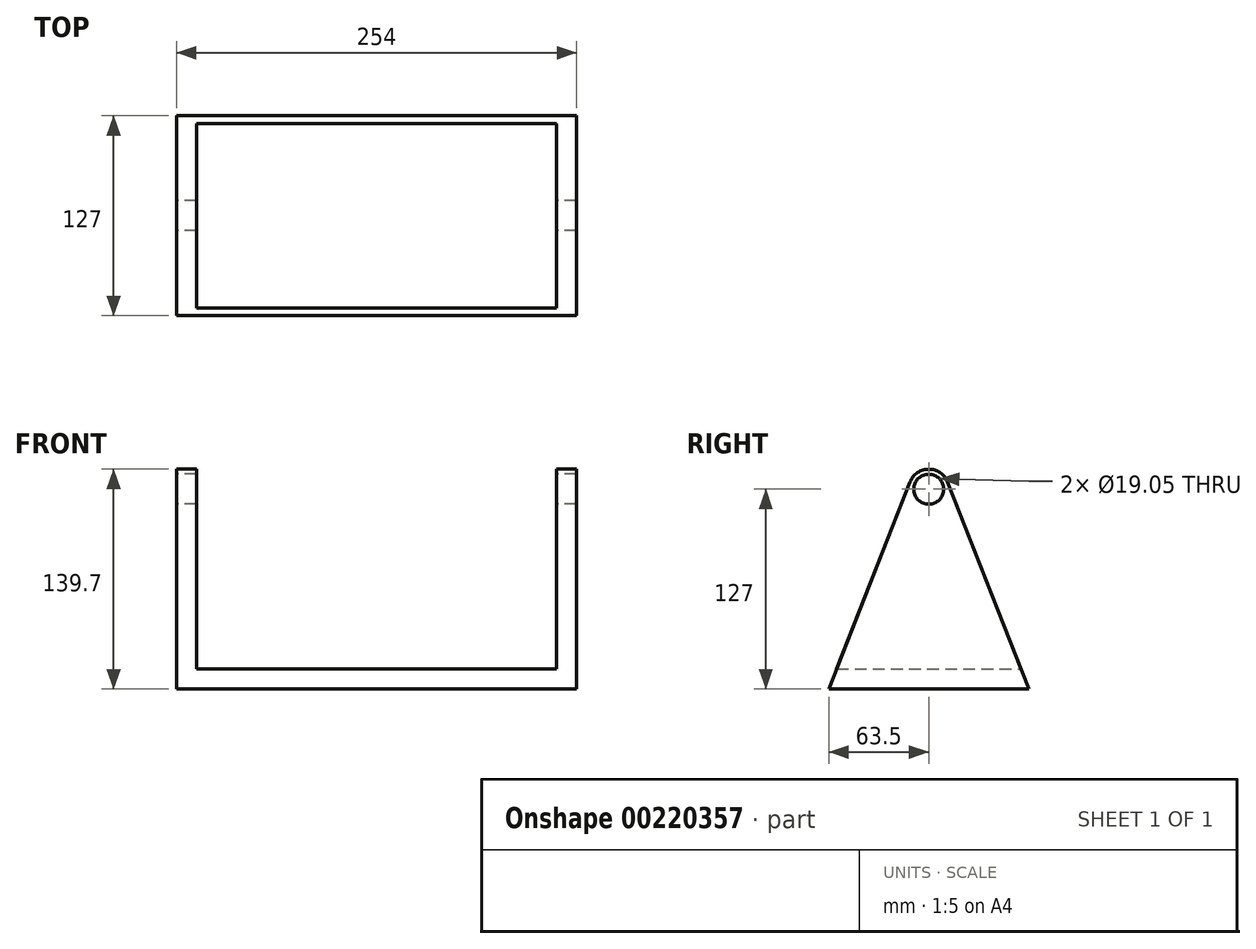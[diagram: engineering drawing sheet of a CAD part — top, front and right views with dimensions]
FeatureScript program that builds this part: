
annotation { "Feature Type Name" : "Feature", "Feature Type Description" : "" }
export const myFeature = defineFeature(function(context is Context, id is Id, definition is map)
    precondition{}
    {
        {
            var Q0;
            Q0=qCreatedBy(makeId("Right.planeOp"),FACE);
            var sketch = newSketch(context, id + "F0", { "sketchPlane" : qUnion([Q0])});
            skCircle(sketch, "E0", {"center": v(0, 0) * mm, "radius": 9.53 * mm});
            skCircle(sketch, "E1", {"center": v(0, 0) * mm, "radius": 12.7 * mm});
            skLineSegment(sketch, "E2", {"start": v(-11.82, 4.64) * mm, "end": v(-63.5, -127) * mm});
            skLineSegment(sketch, "E3", {"start": v(-63.5, -127) * mm, "end": v(63.5, -127) * mm});
            skLineSegment(sketch, "E4", {"start": v(63.5, -127) * mm, "end": v(11.82, 4.64) * mm});
            skSolve(sketch);
        }
        {
            var Q0;
            Q0 = qSketchRegion(id + "F0", true);
            extrude(context, id + "F1", {"entities" : qUnion([Q0]), "endBound" : BoundingType.SYMMETRIC, "depth" : 254 * mm});
        }
        {
            var Q0;
            Q0=qCreatedBy(makeId("Front.planeOp"),FACE);
            var sketch = newSketch(context, id + "F2", { "sketchPlane" : qUnion([Q0])});
            skLineSegment(sketch, "E5.bottom", {"start": v(114.3, 38.1) * mm, "end": v(-114.3, 38.1) * mm});
            skLineSegment(sketch, "E5.top", {"start": v(114.3, -114.3) * mm, "end": v(-114.3, -114.3) * mm});
            skLineSegment(sketch, "E5.left", {"start": v(114.3, 38.1) * mm, "end": v(114.3, -114.3) * mm});
            skLineSegment(sketch, "E5.right", {"start": v(-114.3, 38.1) * mm, "end": v(-114.3, -114.3) * mm});
            skSolve(sketch);
        }
        {
            var Q0;
            Q0 = qSketchRegion(id + "F2", true);
            extrude(context, id + "F3", {"entities" : qUnion([Q0]), "operationType" : NewBodyOperationType.REMOVE, "endBound" : BoundingType.SYMMETRIC, "depth" : 227.08 * mm});
        }
    });
